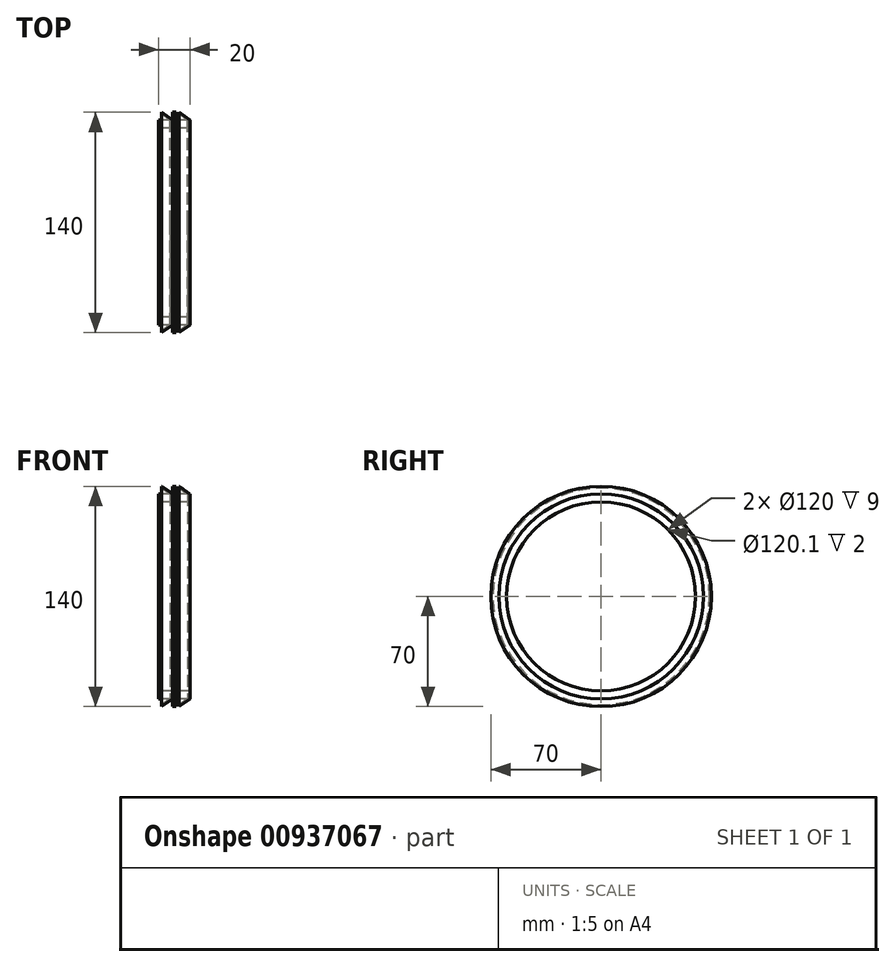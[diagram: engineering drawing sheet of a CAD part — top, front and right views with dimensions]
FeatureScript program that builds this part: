
annotation { "Feature Type Name" : "Feature", "Feature Type Description" : "" }
export const myFeature = defineFeature(function(context is Context, id is Id, definition is map)
    precondition{}
    {
        {
            var Q0;
            Q0=qCreatedBy(makeId("Front.planeOp"),FACE);
            var sketch = newSketch(context, id + "F0", { "sketchPlane" : qUnion([Q0])});
            skLineSegment(sketch, "E0.bottom", {"start": v(-1, 70) * mm, "end": v(1, 70) * mm});
            skLineSegment(sketch, "E0.top", {"start": v(-1, 60.05) * mm, "end": v(1, 60.05) * mm});
            skLineSegment(sketch, "E0.left", {"start": v(-1, 70) * mm, "end": v(-1, 60.05) * mm});
            skLineSegment(sketch, "E0.right", {"start": v(1, 70) * mm, "end": v(1, 60.05) * mm});
            skLineSegment(sketch, "E1", {"start": v(-46.18, 0) * mm, "end": v(62.63, 0) * mm, "construction": true});
            skSolve(sketch);
        }
        {
            var Q0;
            Q0=makeQuery(id+"F0.imprint","IMPRINT",FACE,{"disambiguationData":[TD([[makeQuery(id+"F0.imprint","IMPRINT",EDGE,{"derivedFrom":sQuery(id+"F0.wireOp",EDGE,"E0.bottom")}),-1.0]])]});
            var Q1;
            Q1=sQuery(id+"F0.wireOp",EDGE,"E1");
            revolve(context, id + "F1", {"surfaceOperationType" : NewSurfaceOperationType.NEW, "entities" : qUnion([Q0]), "axis" : qUnion([Q1]), "revolveType" : RevolveType.FULL});
        }
        {
            var Q0;
            Q0=qCreatedBy(makeId("Front.planeOp"),FACE);
            var sketch = newSketch(context, id + "F2", { "sketchPlane" : qUnion([Q0])});
            skLineSegment(sketch, "E2.bottom", {"start": v(-10, 65) * mm, "end": v(-2.72, 65) * mm});
            skLineSegment(sketch, "E2.top", {"start": v(-10, 60) * mm, "end": v(-1, 60) * mm});
            skLineSegment(sketch, "E2.left", {"start": v(-10, 65) * mm, "end": v(-10, 60) * mm});
            skLineSegment(sketch, "E2.right", {"start": v(-1, 65) * mm, "end": v(-1, 60) * mm});
            skLineSegment(sketch, "E3", {"start": v(-1, 65) * mm, "end": v(-8, 70) * mm});
            skLineSegment(sketch, "E4", {"start": v(-8, 68.77) * mm, "end": v(-2.72, 65) * mm});
            skLineSegment(sketch, "E5", {"start": v(-37.45, 0) * mm, "end": v(43.9, 0) * mm, "construction": true});
            skLineSegment(sketch, "E6", {"start": v(-8, 70) * mm, "end": v(-8, 68.77) * mm});
            skLineSegment(sketch, "E7.1.0.0", {"start": v(1, 65) * mm, "end": v(8.28, 65) * mm});
            skLineSegment(sketch, "E7.1.0.1", {"start": v(1, 60) * mm, "end": v(10, 60) * mm});
            skLineSegment(sketch, "E7.1.0.2", {"start": v(10, 65) * mm, "end": v(3, 70) * mm});
            skLineSegment(sketch, "E7.1.0.3", {"start": v(10, 65) * mm, "end": v(10, 60) * mm});
            skLineSegment(sketch, "E7.1.0.4", {"start": v(1, 65) * mm, "end": v(1, 60) * mm});
            skLineSegment(sketch, "E7.1.0.5", {"start": v(3, 70) * mm, "end": v(3, 68.77) * mm});
            skLineSegment(sketch, "E7.1.0.6", {"start": v(3, 68.77) * mm, "end": v(8.28, 65) * mm});
            skLineSegment(sketch, "E7.direction1", {"start": v(-10, 60) * mm, "end": v(1, 60) * mm, "construction": true});
            skSolve(sketch);
        }
        {
            var Q0;
            Q0=makeQuery(id+"F2.imprint","IMPRINT",FACE,{"disambiguationData":[TD([[makeQuery(id+"F2.imprint","IMPRINT",EDGE,{"derivedFrom":sQuery(id+"F2.wireOp",EDGE,"E2.bottom")}),-1.0]])]});
            var Q1;
            Q1=makeQuery(id+"F2.imprint","IMPRINT",FACE,{"disambiguationData":[TD([[makeQuery(id+"F2.imprint","IMPRINT",EDGE,{"derivedFrom":sQuery(id+"F2.wireOp",EDGE,"E7.1.0.0")}),-1.0]])]});
            var Q2;
            Q2=sQuery(id+"F2.wireOp",EDGE,"E5");
            revolve(context, id + "F3", {"operationType" : NewBodyOperationType.ADD, "surfaceOperationType" : NewSurfaceOperationType.NEW, "entities" : qUnion([Q0, Q1]), "axis" : qUnion([Q2]), "revolveType" : RevolveType.FULL});
        }
    });
